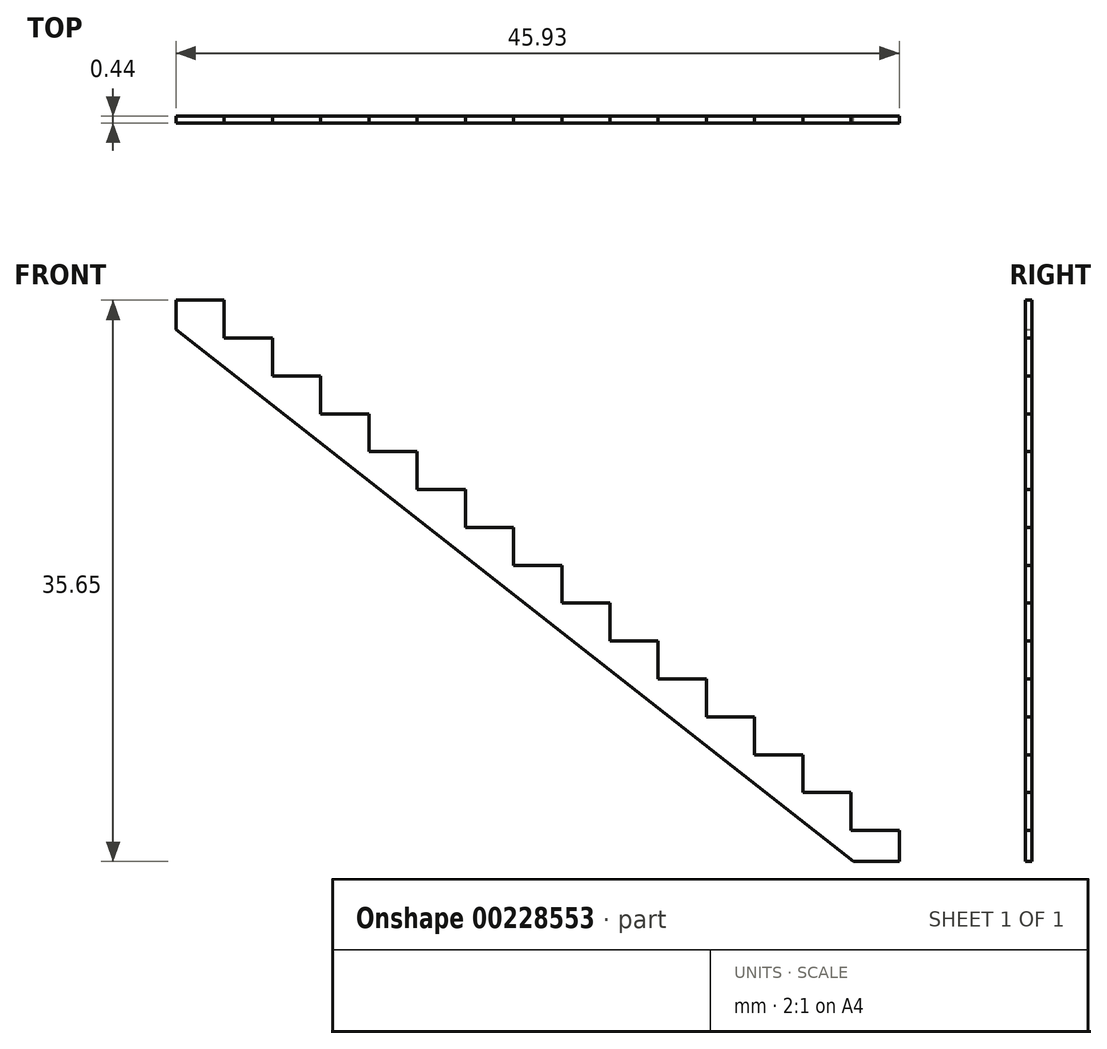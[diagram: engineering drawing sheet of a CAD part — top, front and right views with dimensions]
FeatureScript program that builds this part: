
annotation { "Feature Type Name" : "Feature", "Feature Type Description" : "" }
export const myFeature = defineFeature(function(context is Context, id is Id, definition is map)
    precondition{}
    {
        {
            var Q0;
            Q0=qCreatedBy(makeId("Front.planeOp"),FACE);
            var sketch = newSketch(context, id + "F0", { "sketchPlane" : qUnion([Q0])});
            skLineSegment(sketch, "E0", {"start": v(0, 0) * mm, "end": v(0, 171.45) * mm});
            skLineSegment(sketch, "E1", {"start": v(0, 171.45) * mm, "end": v(-266.7, 171.45) * mm});
            skLineSegment(sketch, "E2", {"start": v(-266.7, 171.45) * mm, "end": v(-266.7, 381) * mm});
            skLineSegment(sketch, "E3", {"start": v(-266.7, 381) * mm, "end": v(-533.4, 381) * mm});
            skLineSegment(sketch, "E4", {"start": v(-533.4, 381) * mm, "end": v(-533.4, 590.55) * mm});
            skLineSegment(sketch, "E5", {"start": v(-533.4, 590.55) * mm, "end": v(-800.1, 590.55) * mm});
            skLineSegment(sketch, "E6", {"start": v(-800.1, 590.55) * mm, "end": v(-800.1, 800.1) * mm});
            skLineSegment(sketch, "E7", {"start": v(-800.1, 800.1) * mm, "end": v(-1066.8, 800.1) * mm});
            skLineSegment(sketch, "E8", {"start": v(-1066.8, 800.1) * mm, "end": v(-1066.8, 1009.65) * mm});
            skLineSegment(sketch, "E9", {"start": v(-1066.8, 1009.65) * mm, "end": v(-1333.5, 1009.65) * mm});
            skLineSegment(sketch, "E10", {"start": v(-1333.5, 1009.65) * mm, "end": v(-1333.5, 1219.2) * mm});
            skLineSegment(sketch, "E11", {"start": v(-1333.5, 1219.2) * mm, "end": v(-1600.2, 1219.2) * mm});
            skLineSegment(sketch, "E12", {"start": v(-1600.2, 1219.2) * mm, "end": v(-1600.2, 1428.75) * mm});
            skLineSegment(sketch, "E13", {"start": v(-1600.2, 1428.75) * mm, "end": v(-1866.9, 1428.75) * mm});
            skLineSegment(sketch, "E14", {"start": v(-1866.9, 1638.3) * mm, "end": v(-2133.6, 1638.3) * mm});
            skLineSegment(sketch, "E15", {"start": v(-2133.6, 1638.3) * mm, "end": v(-2133.6, 1847.85) * mm});
            skLineSegment(sketch, "E16", {"start": v(-2133.6, 1847.85) * mm, "end": v(-2400.3, 1847.85) * mm});
            skLineSegment(sketch, "E17", {"start": v(-2400.3, 1847.85) * mm, "end": v(-2400.3, 2057.4) * mm});
            skLineSegment(sketch, "E18", {"start": v(-2400.3, 2057.4) * mm, "end": v(-2667, 2057.4) * mm});
            skLineSegment(sketch, "E19", {"start": v(-2667, 2057.4) * mm, "end": v(-2667, 2266.95) * mm});
            skLineSegment(sketch, "E20", {"start": v(-2667, 2266.95) * mm, "end": v(-2933.7, 2266.95) * mm});
            skLineSegment(sketch, "E21", {"start": v(-2933.7, 2266.95) * mm, "end": v(-2933.7, 2476.5) * mm});
            skLineSegment(sketch, "E22", {"start": v(-2933.7, 2476.5) * mm, "end": v(-3200.4, 2476.5) * mm});
            skLineSegment(sketch, "E23", {"start": v(-3200.4, 2476.5) * mm, "end": v(-3200.4, 2686.05) * mm});
            skLineSegment(sketch, "E24", {"start": v(-3200.4, 2686.05) * mm, "end": v(-3467.1, 2686.05) * mm});
            skLineSegment(sketch, "E25", {"start": v(-1866.9, 1428.75) * mm, "end": v(-1866.9, 1638.3) * mm});
            skLineSegment(sketch, "E26", {"start": v(-4000.5, 2943.22) * mm, "end": v(-254.58, 0) * mm});
            skLineSegment(sketch, "E27", {"start": v(-254.58, 0) * mm, "end": v(0, 0) * mm});
            skLineSegment(sketch, "E28", {"start": v(-2933.7, 2476.5) * mm, "end": v(-2133.6, 1847.85) * mm, "construction": true});
            skLineSegment(sketch, "E29", {"start": v(-1466.85, 1219.2) * mm, "end": v(-1466.85, 3048) * mm, "construction": true});
            skLineSegment(sketch, "E30", {"start": v(-3467.1, 2686.05) * mm, "end": v(-3467.1, 2895.6) * mm});
            skLineSegment(sketch, "E31", {"start": v(-3467.1, 2895.6) * mm, "end": v(-3733.8, 2895.6) * mm});
            skLineSegment(sketch, "E32", {"start": v(-3733.8, 2895.6) * mm, "end": v(-3733.8, 3105.15) * mm});
            skLineSegment(sketch, "E33", {"start": v(-3733.8, 3105.15) * mm, "end": v(-4000.5, 3105.15) * mm});
            skLineSegment(sketch, "E34", {"start": v(-4000.5, 2943.22) * mm, "end": v(-4000.5, 3105.15) * mm});
            skSolve(sketch);
        }
        {
            var Q0;
            Q0=makeQuery(id+"F0.imprint","IMPRINT",FACE,{"disambiguationData":[TD([[makeQuery(id+"F0.imprint","IMPRINT",EDGE,{"derivedFrom":sQuery(id+"F0.wireOp",EDGE,"E0")}),1.0]])]});
            extrude(context, id + "F1", {"entities" : qUnion([Q0]), "depth" : 38.1 * mm});
        }
        {
            var Q0;
            Q0=makeQuery(id+"F1.opExtrude","SWEPT_BODY",BODY,{"disambiguationData":[OSD([sQuery(id+"F0.wireOp",EDGE,"E0"),sQuery(id+"F0.wireOp",EDGE,"E1"),sQuery(id+"F0.wireOp",EDGE,"E2"),sQuery(id+"F0.wireOp",EDGE,"E3"),sQuery(id+"F0.wireOp",EDGE,"E4"),sQuery(id+"F0.wireOp",EDGE,"E5"),sQuery(id+"F0.wireOp",EDGE,"E6"),sQuery(id+"F0.wireOp",EDGE,"E7"),sQuery(id+"F0.wireOp",EDGE,"E8"),sQuery(id+"F0.wireOp",EDGE,"E9"),sQuery(id+"F0.wireOp",EDGE,"E10"),sQuery(id+"F0.wireOp",EDGE,"E11"),sQuery(id+"F0.wireOp",EDGE,"E12"),sQuery(id+"F0.wireOp",EDGE,"E13"),sQuery(id+"F0.wireOp",EDGE,"E14"),sQuery(id+"F0.wireOp",EDGE,"E15"),sQuery(id+"F0.wireOp",EDGE,"E16"),sQuery(id+"F0.wireOp",EDGE,"E17"),sQuery(id+"F0.wireOp",EDGE,"E18"),sQuery(id+"F0.wireOp",EDGE,"E19"),sQuery(id+"F0.wireOp",EDGE,"E20"),sQuery(id+"F0.wireOp",EDGE,"E21"),sQuery(id+"F0.wireOp",EDGE,"E22"),sQuery(id+"F0.wireOp",EDGE,"E23"),sQuery(id+"F0.wireOp",EDGE,"E24"),sQuery(id+"F0.wireOp",EDGE,"E25"),sQuery(id+"F0.wireOp",EDGE,"E26"),sQuery(id+"F0.wireOp",EDGE,"E27"),sQuery(id+"F0.wireOp",EDGE,"E30"),sQuery(id+"F0.wireOp",EDGE,"E31"),sQuery(id+"F0.wireOp",EDGE,"E32"),sQuery(id+"F0.wireOp",EDGE,"E33"),sQuery(id+"F0.wireOp",EDGE,"E34")])]});
            var Q1;
            Q1=qCreatedBy(makeId("Origin.pointOp"),VERTEX);
            transform(context, id + "F2", {"entities" : qUnion([Q0]), "transformType" : TransformType.SCALE_UNIFORMLY, "scale" : 1 / 87.1, "scalePoint" : qUnion([Q1]), "makeCopy" : false});
        }
    });
